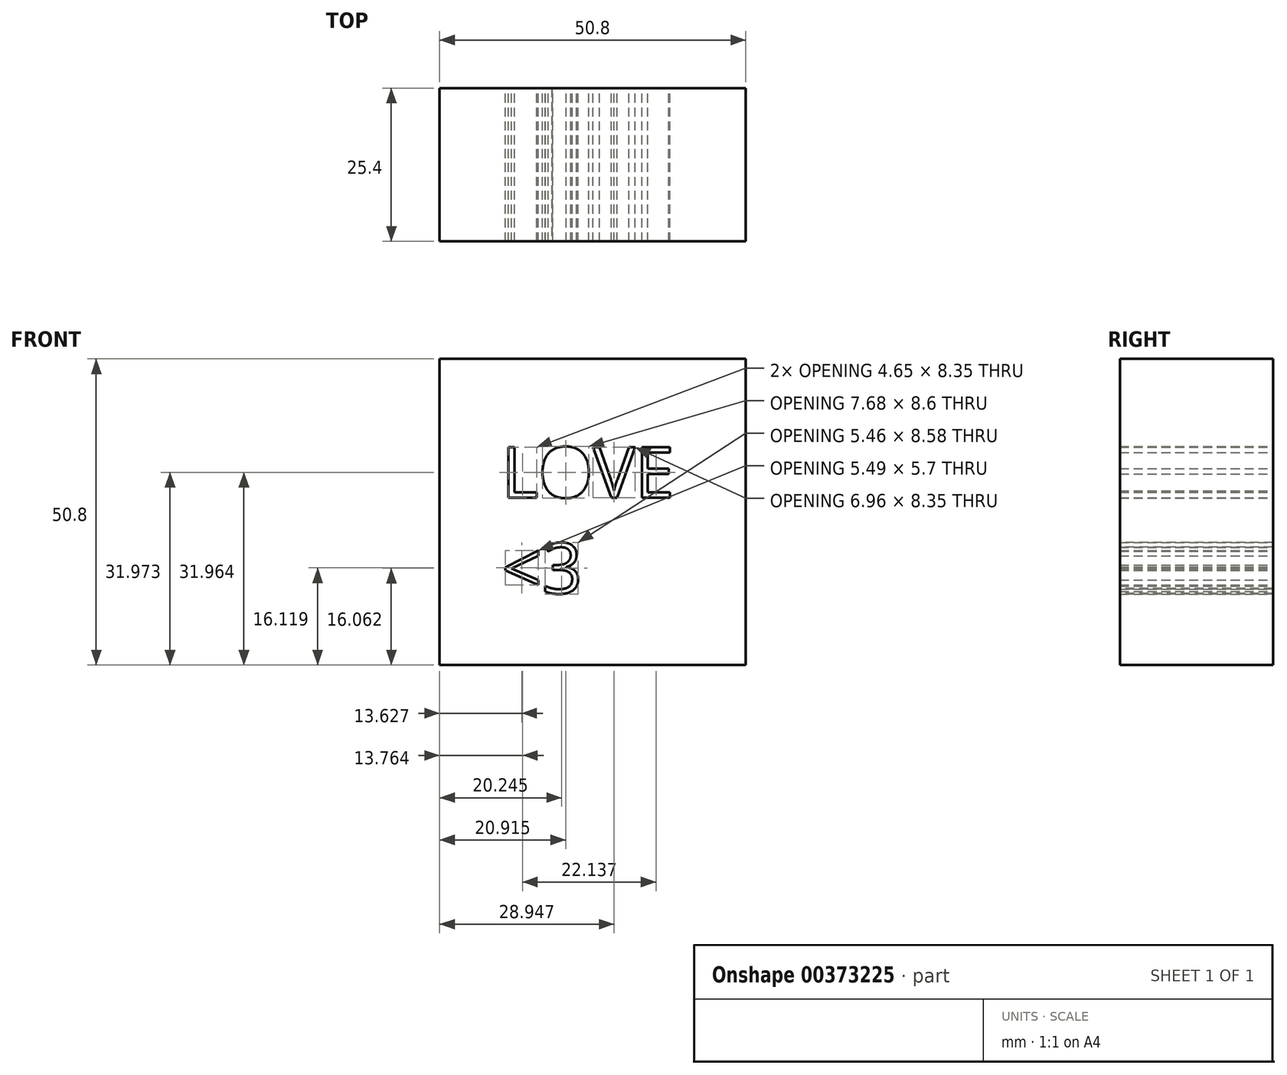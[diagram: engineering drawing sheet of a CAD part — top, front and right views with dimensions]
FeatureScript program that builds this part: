
annotation { "Feature Type Name" : "Feature", "Feature Type Description" : "" }
export const myFeature = defineFeature(function(context is Context, id is Id, definition is map)
    precondition{}
    {
        {
            var Q0;
            Q0=qCreatedBy(makeId("Front.planeOp"),FACE);
            var sketch = newSketch(context, id + "F0", { "sketchPlane" : qUnion([Q0])});
            skLineSegment(sketch, "E0.bottom", {"start": v(-10.29, 35.92) * mm, "end": v(40.51, 35.92) * mm});
            skLineSegment(sketch, "E0.top", {"start": v(-10.29, -14.88) * mm, "end": v(40.51, -14.88) * mm});
            skLineSegment(sketch, "E0.left", {"start": v(-10.29, 35.92) * mm, "end": v(-10.29, -14.88) * mm});
            skLineSegment(sketch, "E0.right", {"start": v(40.51, 35.92) * mm, "end": v(40.51, -14.88) * mm});
            skText(sketch, "E1", { "text": "LOVE \n<3", "fontName": "OpenSans-Regular.ttf"});
            const initialGuessF0  = {"E1": [0, 0.01291, 1, 0, 0.00842]};
            skSetInitialGuess(sketch, initialGuessF0);
            skSolve(sketch);
        }
        {
            var Q0;
            Q0=makeQuery(id+"F0.imprint","IMPRINT",FACE,{"disambiguationData":[TD([[makeQuery(id+"F0.imprint","IMPRINT",EDGE,{"derivedFrom":sQuery(id+"F0.wireOp",EDGE,"E0.bottom")}),-1.0]])]});
            extrude(context, id + "F1", {"entities" : qUnion([Q0]), "depth" : 25.4 * mm});
        }
    });
